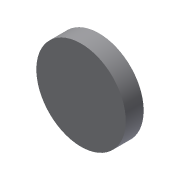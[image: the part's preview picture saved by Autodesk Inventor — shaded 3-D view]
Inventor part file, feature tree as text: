
AUTODESK INVENTOR PART (.ipt)
format: ipt  version: 2019.4 (Build 234330000, 330)  size: 75,776 bytes
history: native  units: mm
features: extrude x1, sketch x1
ambient origin geometry x8: Origin, YZ Plane, XZ Plane, XY Plane, X Axis, Y Axis, Z Axis, Center Point
bodies: Solid1 (feature_tree)
feature tree (2):
  extrude  "Extrusion1"  Depth=2.0mm TaperAngle=0.0deg
  sketch  "Sketch1"  dims[d0=10.0mm d1=2.0mm d2=0.0mm]
